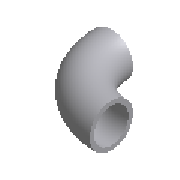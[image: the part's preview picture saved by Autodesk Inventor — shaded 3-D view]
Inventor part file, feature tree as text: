
AUTODESK INVENTOR PART (.ipt)
format: ipt  version: 2025.1 (Build 291241020, 241B)  size: 180,736 bytes
history: native  units: mm (DEFAULTED — no unit token found)
features: other x4, sweep x1
ambient origin geometry x8: Origin, YZ Plane, XZ Plane, XY Plane, X Axis, Y Axis, Z Axis, Center Point
bodies: Solid1 (feature_tree)
feature tree (5):
  sweep  "Sweep1"
  other  "Work Point1"
  other  "Work Point2"
  other  "Work Axis1"
  other  "Work Axis2"
